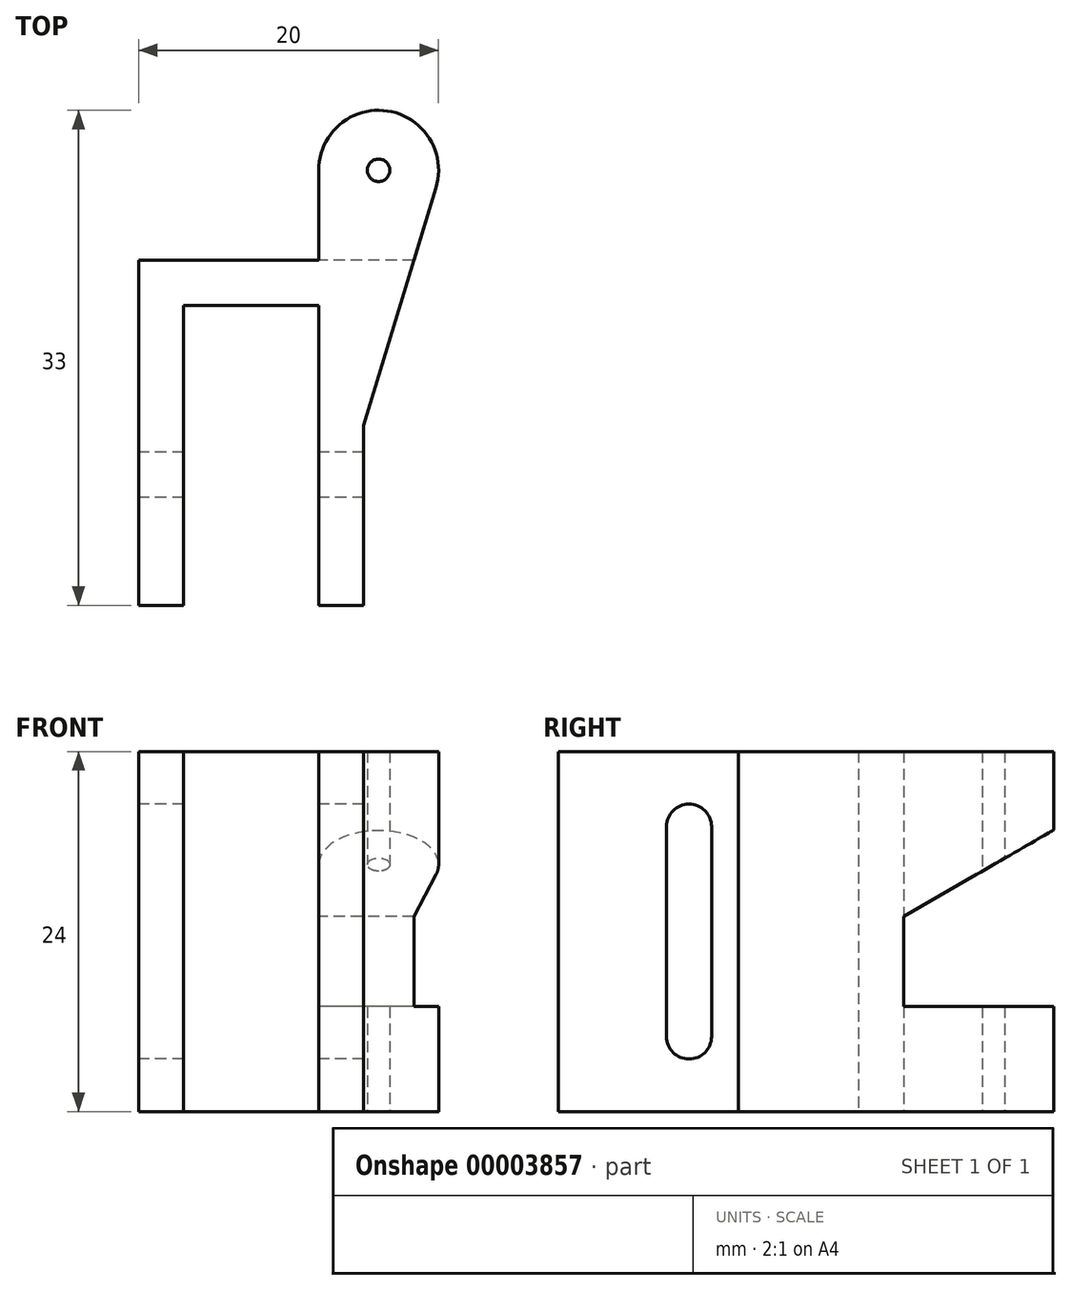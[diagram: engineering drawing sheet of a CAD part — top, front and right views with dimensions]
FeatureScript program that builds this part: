
annotation { "Feature Type Name" : "Feature", "Feature Type Description" : "" }
export const myFeature = defineFeature(function(context is Context, id is Id, definition is map)
    precondition{}
    {
        {
            var Q0;
            Q0=qCreatedBy(makeId("Top.planeOp"),FACE);
            var sketch = newSketch(context, id + "F0", { "sketchPlane" : qUnion([Q0])});
            skLineSegment(sketch, "E0", {"start": v(-92.53, -5.67) * mm, "end": v(-95.53, -5.67) * mm});
            skLineSegment(sketch, "E1", {"start": v(-95.53, -5.67) * mm, "end": v(-95.53, 14.33) * mm});
            skLineSegment(sketch, "E2", {"start": v(-95.53, 14.33) * mm, "end": v(-104.53, 14.33) * mm});
            skLineSegment(sketch, "E3", {"start": v(-104.53, 14.33) * mm, "end": v(-104.53, -5.67) * mm});
            skLineSegment(sketch, "E4", {"start": v(-104.53, -5.67) * mm, "end": v(-107.53, -5.67) * mm});
            skCircle(sketch, "E5", {"center": v(-91.53, 23.33) * mm, "radius": 0.75 * mm});
            skArc(sketch, "E6", {"start": v(-87.7, 22.16) * mm, "mid": v(-90.94, 27.29) * mm, "end": v(-95.53, 23.33) * mm});
            skLineSegment(sketch, "E7", {"start": v(-107.53, -5.67) * mm, "end": v(-107.53, 17.33) * mm});
            skLineSegment(sketch, "E8", {"start": v(-95.53, 17.33) * mm, "end": v(-95.53, 23.33) * mm});
            skLineSegment(sketch, "E9", {"start": v(-107.53, 17.33) * mm, "end": v(-95.53, 17.33) * mm});
            skLineSegment(sketch, "E10", {"start": v(-92.53, -5.67) * mm, "end": v(-92.53, 6.33) * mm});
            skLineSegment(sketch, "E11", {"start": v(-92.53, 6.33) * mm, "end": v(-87.7, 22.16) * mm});
            skSolve(sketch);
        }
        {
            var Q0;
            Q0=makeQuery(id+"F0.imprint","IMPRINT",FACE,{"disambiguationData":[TD([[makeQuery(id+"F0.imprint","IMPRINT",EDGE,{"derivedFrom":sQuery(id+"F0.wireOp",EDGE,"E0")}),-1.0]])]});
            extrude(context, id + "F1", {"entities" : qUnion([Q0]), "depth" : 24 * mm});
        }
        {
            var Q0;
            Q0=makeQuery(id+"F1.opExtrude","SWEPT_FACE",FACE,{"disambiguationData":[OSD([sQuery(id+"F0.wireOp",EDGE,"E8")])]});
            var sketch = newSketch(context, id + "F2", { "sketchPlane" : qUnion([Q0])});
            skLineSegment(sketch, "E12", {"start": v(-17.33, 7) * mm, "end": v(-32.8, 7) * mm});
            skLineSegment(sketch, "E13", {"start": v(-32.8, 7) * mm, "end": v(-32.8, 21.93) * mm});
            skLineSegment(sketch, "E14", {"start": v(-32.8, 21.93) * mm, "end": v(-17.33, 13) * mm});
            skLineSegment(sketch, "E15", {"start": v(-17.33, 13) * mm, "end": v(-17.33, 7) * mm});
            skSolve(sketch);
        }
        {
            var Q0;
            {var subQ7=sQuery(id+"F2.wireOp",EDGE,"E13");var subQ8=sQuery(id+"F2.wireOp",EDGE,"E15");Q0=qUnion([makeQuery(id+"F2.imprint","IMPRINT",FACE,{"disambiguationData":[TD([[makeQuery(id+"F2.imprint","IMPRINT",EDGE,{"derivedFrom":subQ7}),-1.0]])]}),makeQuery(id+"F2.imprint","IMPRINT",FACE,{"disambiguationData":[TD([[makeQuery(id+"F2.imprint","IMPRINT",EDGE,{"derivedFrom":subQ8}),-1.0]])]})]);}
            extrude(context, id + "F3", {"entities" : qUnion([Q0]), "operationType" : NewBodyOperationType.REMOVE, "endBound" : BoundingType.UP_TO_NEXT, "oppositeDirection" : true, "depth" : 25 * mm});
        }
        {
            var Q0;
            {var subQ7=sQuery(id+"F2.wireOp",EDGE,"E13");var subQ8=sQuery(id+"F2.wireOp",EDGE,"E15");Q0=qUnion([makeQuery(id+"F2.imprint","IMPRINT",FACE,{"disambiguationData":[TD([[makeQuery(id+"F2.imprint","IMPRINT",EDGE,{"derivedFrom":subQ7}),-1.0]])]}),makeQuery(id+"F2.imprint","IMPRINT",FACE,{"disambiguationData":[TD([[makeQuery(id+"F2.imprint","IMPRINT",EDGE,{"derivedFrom":subQ8}),-1.0]])]})]);}
            extrude(context, id + "F4", {"entities" : qUnion([Q0]), "operationType" : NewBodyOperationType.REMOVE, "oppositeDirection" : true, "depth" : 25 * mm});
        }
        {
            var Q0;
            Q0=makeQuery(id+"F1.opExtrude","SWEPT_FACE",FACE,{"disambiguationData":[OSD([sQuery(id+"F0.wireOp",EDGE,"E7")])]});
            var sketch = newSketch(context, id + "F5", { "sketchPlane" : qUnion([Q0])});
            skArc(sketch, "E16", {"start": v(-1.53, 19) * mm, "mid": v(-3.03, 20.5) * mm, "end": v(-4.53, 19) * mm});
            skArc(sketch, "E17", {"start": v(-4.53, 5) * mm, "mid": v(-3.03, 3.5) * mm, "end": v(-1.53, 5) * mm});
            skLineSegment(sketch, "E18", {"start": v(-4.53, 19) * mm, "end": v(-4.53, 5) * mm});
            skLineSegment(sketch, "E19", {"start": v(-4.53, 5) * mm, "end": v(-1.53, 5) * mm});
            skLineSegment(sketch, "E20", {"start": v(-1.53, 5) * mm, "end": v(-1.53, 19) * mm});
            skSolve(sketch);
        }
        {
            var Q0;
            {Q0=qUnion([makeQuery(id+"F5.imprint","IMPRINT",FACE,{"disambiguationData":[TD([[makeQuery(id+"F5.imprint","IMPRINT",EDGE,{"derivedFrom":sQuery(id+"F5.wireOp",EDGE,"E16")}),1.0]])]}),makeQuery(id+"F5.imprint","IMPRINT",FACE,{"disambiguationData":[TD([[makeQuery(id+"F5.imprint","IMPRINT",EDGE,{"derivedFrom":sQuery(id+"F5.wireOp",EDGE,"E17")}),1.0]])]})]);}
            extrude(context, id + "F6", {"entities" : qUnion([Q0]), "operationType" : NewBodyOperationType.REMOVE, "oppositeDirection" : true, "depth" : 25 * mm});
        }
    });
